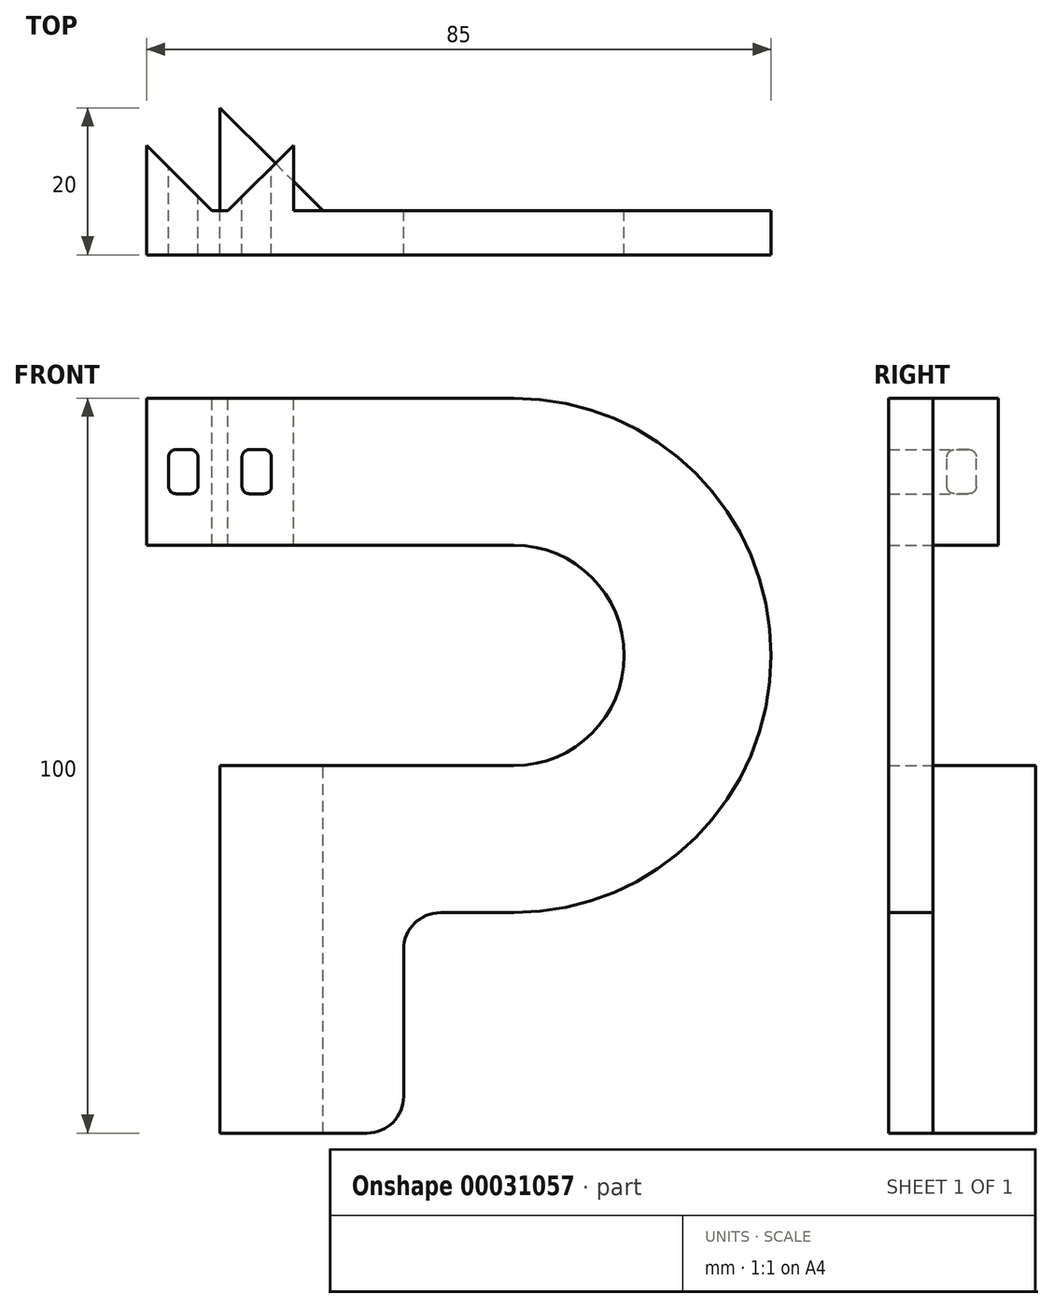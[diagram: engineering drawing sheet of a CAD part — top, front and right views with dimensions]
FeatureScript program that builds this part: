
annotation { "Feature Type Name" : "Feature", "Feature Type Description" : "" }
export const myFeature = defineFeature(function(context is Context, id is Id, definition is map)
    precondition{}
    {
        {
            var Q0;
            Q0=qCreatedBy(makeId("Front.planeOp"),FACE);
            var sketch = newSketch(context, id + "F0", { "sketchPlane" : qUnion([Q0])});
            skLineSegment(sketch, "E0.bottom", {"start": v(0, -15) * mm, "end": v(25, -15) * mm});
            skLineSegment(sketch, "E0.top", {"start": v(0, -65) * mm, "end": v(25, -65) * mm});
            skLineSegment(sketch, "E0.left", {"start": v(0, -15) * mm, "end": v(0, -65) * mm});
            skLineSegment(sketch, "E0.right", {"start": v(25, -15) * mm, "end": v(25, -65) * mm});
            skCircle(sketch, "E1", {"center": v(40, 0) * mm, "radius": 15 * mm});
            skLineSegment(sketch, "E2", {"start": v(25, -15) * mm, "end": v(40, -15) * mm});
            skCircle(sketch, "E3", {"center": v(40, 0) * mm, "radius": 35 * mm});
            skLineSegment(sketch, "E4", {"start": v(40, -35) * mm, "end": v(25, -35) * mm});
            skLineSegment(sketch, "E5", {"start": v(40, 15) * mm, "end": v(-10, 15) * mm});
            skLineSegment(sketch, "E6", {"start": v(-10, 15) * mm, "end": v(-10, 35) * mm});
            skLineSegment(sketch, "E7", {"start": v(-10, 35) * mm, "end": v(40, 35) * mm});
            skPoint(sketch, "E8", {"position": v(-10, 25) * mm});
            skLineSegment(sketch, "E9", {"start": v(-10, 25) * mm, "end": v(40, 25) * mm, "construction": true});
            skLineSegment(sketch, "E10", {"start": v(-7, 25) * mm, "end": v(-7, 28) * mm});
            skLineSegment(sketch, "E11", {"start": v(-7, 28) * mm, "end": v(-3, 28) * mm});
            skLineSegment(sketch, "E12", {"start": v(-3, 28) * mm, "end": v(-3, 25) * mm});
            skLineSegment(sketch, "E13.MirrorCS", {"start": v(-7, 25) * mm, "end": v(-7, 22) * mm});
            skLineSegment(sketch, "E14.MirrorCS", {"start": v(-7, 22) * mm, "end": v(-3, 22) * mm});
            skLineSegment(sketch, "E15.MirrorCS", {"start": v(-3, 22) * mm, "end": v(-3, 25) * mm});
            skLineSegment(sketch, "E16.MirrorCS", {"start": v(3, 22) * mm, "end": v(3, 25) * mm});
            skLineSegment(sketch, "E17.MirrorCS", {"start": v(3, 28) * mm, "end": v(3, 25) * mm});
            skLineSegment(sketch, "E18.MirrorCS", {"start": v(7, 28) * mm, "end": v(3, 28) * mm});
            skLineSegment(sketch, "E19.MirrorCS", {"start": v(7, 25) * mm, "end": v(7, 28) * mm});
            skLineSegment(sketch, "E20.MirrorCS", {"start": v(7, 25) * mm, "end": v(7, 22) * mm});
            skLineSegment(sketch, "E21.MirrorCS", {"start": v(7, 22) * mm, "end": v(3, 22) * mm});
            skSolve(sketch);
        }
        {
            var Q0;
            {var subQ1=sQuery(id+"F0.wireOp",EDGE,"E6");Q0=makeQuery(id+"F0.imprint","IMPRINT",FACE,{"disambiguationData":[TD([[makeQuery(id+"F0.imprint","IMPRINT",EDGE,{"derivedFrom":subQ1}),-1.0]])]});}
            var Q1;
            {var subQ9=sQuery(id+"F0.wireOp",EDGE,"E2");Q1=makeQuery(id+"F0.imprint","IMPRINT",FACE,{"disambiguationData":[TD([[makeQuery(id+"F0.imprint","IMPRINT",EDGE,{"derivedFrom":subQ9}),-1.0]])]});}
            var Q2;
            {var subQ0=sQuery(id+"F0.wireOp",EDGE,"E3");var subQ3=sQuery(id+"F0.wireOp",EDGE,"E0.bottom");var subQ4=makeQuery(id+"F0.imprint","INTERSECT",VERTEX,{"derivedFrom":[subQ3,subQ0]});Q2=makeQuery(id+"F0.imprint","IMPRINT",FACE,{"disambiguationData":[TD([[makeQuery(id+"F0.imprint","IMPRINT",EDGE,{"disambiguationData":[TD([[subQ4,-1.0]])],"derivedFrom":subQ0}),1.0]])]});}
            var Q3;
            {var subQ2=sQuery(id+"F0.wireOp",EDGE,"E0.top");Q3=makeQuery(id+"F0.imprint","IMPRINT",FACE,{"disambiguationData":[TD([[makeQuery(id+"F0.imprint","IMPRINT",EDGE,{"derivedFrom":subQ2}),1.0]])]});}
            var Q4;
            {var subQ0=sQuery(id+"F0.wireOp",EDGE,"E4");Q4=makeQuery(id+"F0.imprint","IMPRINT",FACE,{"disambiguationData":[TD([[makeQuery(id+"F0.imprint","IMPRINT",EDGE,{"derivedFrom":subQ0}),-1.0]])]});}
            extrude(context, id + "F1", {"entities" : qUnion([Q0, Q1, Q2, Q3, Q4]), "depth" : 6 * mm});
        }
        {
            var Q0;
            Q0=makeQuery(id+"F1.opExtrude","SWEPT_FACE",FACE,{"disambiguationData":[OSD([sQuery(id+"F0.wireOp",EDGE,"E0.bottom"),sQuery(id+"F0.wireOp",EDGE,"E2")])]});
            var sketch = newSketch(context, id + "F2", { "sketchPlane" : qUnion([Q0])});
            skLineSegment(sketch, "E22.0.0", {"start": v(40, 0) * mm, "end": v(0, 0) * mm});
            skLineSegment(sketch, "E22.0.1", {"start": v(0, 0) * mm, "end": v(0, -6) * mm});
            skLineSegment(sketch, "E22.0.2", {"start": v(0, -6) * mm, "end": v(40, -6) * mm});
            skLineSegment(sketch, "E22.0.3", {"start": v(40, -6) * mm, "end": v(40, 0) * mm});
            skLineSegment(sketch, "E22.1", {"start": v(0, -6) * mm, "end": v(40, -6) * mm});
            skLineSegment(sketch, "E23", {"start": v(0, 0) * mm, "end": v(0, 14) * mm});
            skLineSegment(sketch, "E24", {"start": v(0, 14) * mm, "end": v(14, 0) * mm});
            skSolve(sketch);
        }
        {
            var Q0;
            {var subQ1=sQuery(id+"F2.wireOp",EDGE,"E23");Q0=makeQuery(id+"F2.imprint","IMPRINT",FACE,{"disambiguationData":[TD([[makeQuery(id+"F2.imprint","IMPRINT",EDGE,{"derivedFrom":subQ1}),-1.0]])]});}
            extrude(context, id + "F3", {"entities" : qUnion([Q0]), "operationType" : NewBodyOperationType.ADD, "oppositeDirection" : true, "depth" : 50 * mm});
        }
        {
            var Q0;
            Q0=makeQuery(id+"F1.opExtrude","SWEPT_FACE",FACE,{"disambiguationData":[OSD([sQuery(id+"F0.wireOp",EDGE,"E7")])]});
            var sketch = newSketch(context, id + "F4", { "sketchPlane" : qUnion([Q0])});
            skLineSegment(sketch, "E25.0", {"start": v(-10, 0) * mm, "end": v(40, 0) * mm});
            skLineSegment(sketch, "E26.0", {"start": v(-10, -6) * mm, "end": v(-10, 0) * mm});
            skLineSegment(sketch, "E27.0", {"start": v(-10, -6) * mm, "end": v(40, -6) * mm});
            skCircle(sketch, "E28", {"center": v(0, 6) * mm, "radius": 5 * mm, "construction": true});
            skLineSegment(sketch, "E29", {"start": v(-10, 8.93) * mm, "end": v(0, -1.07) * mm});
            skLineSegment(sketch, "E30", {"start": v(0, -1.07) * mm, "end": v(10, 8.93) * mm});
            skLineSegment(sketch, "E31", {"start": v(-10, 0) * mm, "end": v(-10, 8.93) * mm});
            skLineSegment(sketch, "E32", {"start": v(10, 8.93) * mm, "end": v(10, 0) * mm});
            skSolve(sketch);
        }
        {
            var Q0;
            {var subQ0=sQuery(id+"F4.wireOp",EDGE,"E31");Q0=makeQuery(id+"F4.imprint","IMPRINT",FACE,{"disambiguationData":[TD([[makeQuery(id+"F4.imprint","IMPRINT",EDGE,{"derivedFrom":subQ0}),-1.0]])]});}
            var Q1;
            {var subQ0=sQuery(id+"F4.wireOp",EDGE,"E32");Q1=makeQuery(id+"F4.imprint","IMPRINT",FACE,{"disambiguationData":[TD([[makeQuery(id+"F4.imprint","IMPRINT",EDGE,{"derivedFrom":subQ0}),-1.0]])]});}
            var Q2;
            Q2=makeQuery(id+"F1.opExtrude","SWEPT_FACE",FACE,{"disambiguationData":[OSD([sQuery(id+"F0.wireOp",EDGE,"E5")])]});
            extrude(context, id + "F5", {"entities" : qUnion([Q0, Q1]), "operationType" : NewBodyOperationType.ADD, "endBound" : BoundingType.UP_TO_SURFACE, "oppositeDirection" : true, "endBoundEntityFace" : qUnion([Q2]), "depth" : 25 * mm});
        }
        {
            var Q0;
            Q0=makeQuery(id+"F1.opExtrude","SWEPT_EDGE",EDGE,{"disambiguationData":[OSD([sQuery(id+"F0.wireOp",EDGE,"E0.right"),sQuery(id+"F0.wireOp",EDGE,"E4")])]});
            var Q1;
            Q1=makeQuery(id+"F1.opExtrude","SWEPT_EDGE",EDGE,{"disambiguationData":[OSD([sQuery(id+"F0.wireOp",EDGE,"E0.top"),sQuery(id+"F0.wireOp",EDGE,"E0.right")])]});
            var Q2;
            Q2=makeQuery(id+"F5.opExtrude","SWEPT_EDGE",EDGE,{"disambiguationData":[OSD([sQuery(id+"F4.wireOp",EDGE,"E25.0"),sQuery(id+"F4.wireOp",EDGE,"E32")])]});
            var Q3;
            Q3=makeQuery(id+"F3.opExtrude","SWEPT_EDGE",EDGE,{"disambiguationData":[OSD([sQuery(id+"F2.wireOp",EDGE,"E22.0.0"),sQuery(id+"F2.wireOp",EDGE,"E24")])]});
            fillet(context, id + "F6", {"entities" : qUnion([Q0, Q1, Q2, Q3]), "radius" : 5 * mm, "tangentPropagation" : true, "allowEdgeOverflow" : false});
        }
        {
            var Q0;
            Q0=makeQuery(id+"F0.imprint","IMPRINT",FACE,{"disambiguationData":[TD([[makeQuery(id+"F0.imprint","IMPRINT",EDGE,{"derivedFrom":sQuery(id+"F0.wireOp",EDGE,"E10")}),-1.0]])]});
            var Q1;
            Q1=makeQuery(id+"F0.imprint","IMPRINT",FACE,{"disambiguationData":[TD([[makeQuery(id+"F0.imprint","IMPRINT",EDGE,{"derivedFrom":sQuery(id+"F0.wireOp",EDGE,"E16.MirrorCS")}),-1.0]])]});
            extrude(context, id + "F7", {"entities" : qUnion([Q0, Q1]), "operationType" : NewBodyOperationType.REMOVE, "endBound" : BoundingType.THROUGH_ALL, "oppositeDirection" : true, "depth" : 25 * mm});
        }
        {
            var Q0;
            {var subQ0=sQuery(id+"F0.wireOp",EDGE,"E20.MirrorCS");var subQ1=sQuery(id+"F0.wireOp",EDGE,"E21.MirrorCS");Q0=makeQuery(id+"F7.boolean.opBoolean","MERGE",EDGE,{"derivedFrom":[makeQuery(id+"F1.opExtrude","SWEPT_EDGE",EDGE,{"disambiguationData":[OSD([subQ0,subQ1])]}),makeQuery(id+"F7.opExtrude","SWEPT_EDGE",EDGE,{"disambiguationData":[OSD([subQ0,subQ1])]})]});}
            var Q1;
            {var subQ0=sQuery(id+"F0.wireOp",EDGE,"E14.MirrorCS");var subQ1=sQuery(id+"F0.wireOp",EDGE,"E15.MirrorCS");Q1=makeQuery(id+"F7.boolean.opBoolean","MERGE",EDGE,{"derivedFrom":[makeQuery(id+"F1.opExtrude","SWEPT_EDGE",EDGE,{"disambiguationData":[OSD([subQ0,subQ1])]}),makeQuery(id+"F7.opExtrude","SWEPT_EDGE",EDGE,{"disambiguationData":[OSD([subQ0,subQ1])]})]});}
            var Q2;
            {var subQ0=sQuery(id+"F0.wireOp",EDGE,"E18.MirrorCS");var subQ1=sQuery(id+"F0.wireOp",EDGE,"E19.MirrorCS");Q2=makeQuery(id+"F7.boolean.opBoolean","MERGE",EDGE,{"derivedFrom":[makeQuery(id+"F1.opExtrude","SWEPT_EDGE",EDGE,{"disambiguationData":[OSD([subQ0,subQ1])]}),makeQuery(id+"F7.opExtrude","SWEPT_EDGE",EDGE,{"disambiguationData":[OSD([subQ0,subQ1])]})]});}
            var Q3;
            {var subQ0=sQuery(id+"F0.wireOp",EDGE,"E11");var subQ1=sQuery(id+"F0.wireOp",EDGE,"E12");Q3=makeQuery(id+"F7.boolean.opBoolean","MERGE",EDGE,{"derivedFrom":[makeQuery(id+"F1.opExtrude","SWEPT_EDGE",EDGE,{"disambiguationData":[OSD([subQ0,subQ1])]}),makeQuery(id+"F7.opExtrude","SWEPT_EDGE",EDGE,{"disambiguationData":[OSD([subQ0,subQ1])]})]});}
            var Q4;
            {var subQ0=sQuery(id+"F0.wireOp",EDGE,"E10");var subQ1=sQuery(id+"F0.wireOp",EDGE,"E11");Q4=makeQuery(id+"F7.boolean.opBoolean","MERGE",EDGE,{"derivedFrom":[makeQuery(id+"F1.opExtrude","SWEPT_EDGE",EDGE,{"disambiguationData":[OSD([subQ0,subQ1])]}),makeQuery(id+"F7.opExtrude","SWEPT_EDGE",EDGE,{"disambiguationData":[OSD([subQ0,subQ1])]})]});}
            var Q5;
            {var subQ0=sQuery(id+"F0.wireOp",EDGE,"E17.MirrorCS");var subQ1=sQuery(id+"F0.wireOp",EDGE,"E18.MirrorCS");Q5=makeQuery(id+"F7.boolean.opBoolean","MERGE",EDGE,{"derivedFrom":[makeQuery(id+"F1.opExtrude","SWEPT_EDGE",EDGE,{"disambiguationData":[OSD([subQ0,subQ1])]}),makeQuery(id+"F7.opExtrude","SWEPT_EDGE",EDGE,{"disambiguationData":[OSD([subQ0,subQ1])]})]});}
            var Q6;
            {var subQ0=sQuery(id+"F0.wireOp",EDGE,"E13.MirrorCS");var subQ1=sQuery(id+"F0.wireOp",EDGE,"E14.MirrorCS");Q6=makeQuery(id+"F7.boolean.opBoolean","MERGE",EDGE,{"derivedFrom":[makeQuery(id+"F1.opExtrude","SWEPT_EDGE",EDGE,{"disambiguationData":[OSD([subQ0,subQ1])]}),makeQuery(id+"F7.opExtrude","SWEPT_EDGE",EDGE,{"disambiguationData":[OSD([subQ0,subQ1])]})]});}
            var Q7;
            {var subQ0=sQuery(id+"F0.wireOp",EDGE,"E16.MirrorCS");var subQ1=sQuery(id+"F0.wireOp",EDGE,"E21.MirrorCS");Q7=makeQuery(id+"F7.boolean.opBoolean","MERGE",EDGE,{"derivedFrom":[makeQuery(id+"F1.opExtrude","SWEPT_EDGE",EDGE,{"disambiguationData":[OSD([subQ0,subQ1])]}),makeQuery(id+"F7.opExtrude","SWEPT_EDGE",EDGE,{"disambiguationData":[OSD([subQ0,subQ1])]})]});}
            fillet(context, id + "F8", {"entities" : qUnion([Q0, Q1, Q2, Q3, Q4, Q5, Q6, Q7]), "radius" : 1 * mm, "tangentPropagation" : true, "allowEdgeOverflow" : false});
        }
    });
